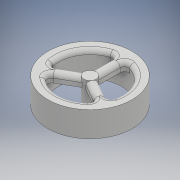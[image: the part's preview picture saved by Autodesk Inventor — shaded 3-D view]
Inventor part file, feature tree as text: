
AUTODESK INVENTOR PART (.ipt)
format: ipt  version: 2018 (Build 220112000, 112)  size: 210,432 bytes
history: native  units: mm
features: extrude x2, fillet x2, sketch x2
ambient origin geometry x8: Origin, YZ Plane, XZ Plane, XY Plane, X Axis, Y Axis, Z Axis, Center Point
bodies: Solido1 (feature_tree)
feature tree (6):
  extrude  "Estrusione1"  Depth=100.0mm
  extrude  "Estrusione2"  Depth=75.0mm
  fillet  "Raccordo1"  Radius=15.0mm
  fillet  "Raccordo2"  Radius=30.0mm
  sketch  "Schizzo1"
  sketch  "Schizzo2"
